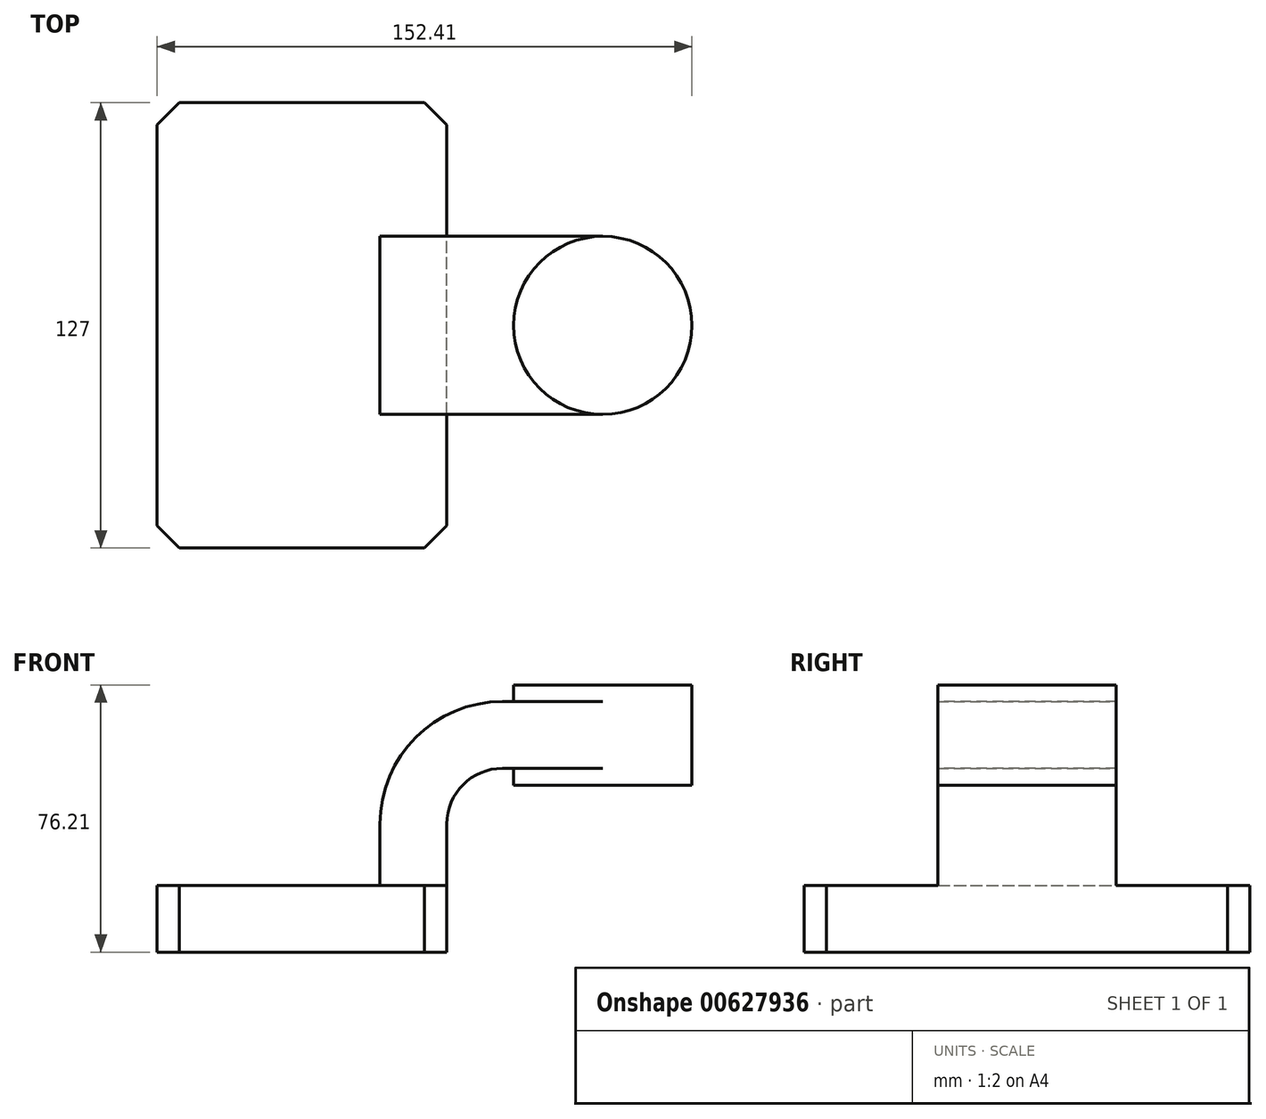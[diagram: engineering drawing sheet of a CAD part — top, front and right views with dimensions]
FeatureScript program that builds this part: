
annotation { "Feature Type Name" : "Feature", "Feature Type Description" : "" }
export const myFeature = defineFeature(function(context is Context, id is Id, definition is map)
    precondition{}
    {
        {
            var Q0;
            Q0=qCreatedBy(makeId("Front.planeOp"),FACE);
            var sketch = newSketch(context, id + "F0", { "sketchPlane" : qUnion([Q0])});
            skLineSegment(sketch, "E0.bottom", {"start": v(-41.28, -9.53) * mm, "end": v(41.28, -9.53) * mm});
            skLineSegment(sketch, "E0.top", {"start": v(-41.28, 9.53) * mm, "end": v(41.28, 9.53) * mm});
            skLineSegment(sketch, "E0.left", {"start": v(-41.28, -9.53) * mm, "end": v(-41.28, 9.53) * mm});
            skLineSegment(sketch, "E0.right", {"start": v(41.28, -9.53) * mm, "end": v(41.28, 9.53) * mm});
            skPoint(sketch, "E0.middle", {"position": v(0, 0) * mm});
            skLineSegment(sketch, "E1.bottom", {"start": v(60.33, 38.1) * mm, "end": v(111.13, 38.1) * mm});
            skLineSegment(sketch, "E1.top", {"start": v(60.33, 66.67) * mm, "end": v(111.12, 66.67) * mm});
            skLineSegment(sketch, "E1.left", {"start": v(60.33, 38.1) * mm, "end": v(60.33, 66.67) * mm});
            skLineSegment(sketch, "E1.right", {"start": v(111.12, 38.1) * mm, "end": v(111.12, 66.67) * mm});
            skPoint(sketch, "E1.middle", {"position": v(85.73, 52.39) * mm});
            skLineSegment(sketch, "E2", {"start": v(41.27, 9.53) * mm, "end": v(41.27, 27) * mm});
            skArc(sketch, "E3", {"start": v(41.27, 27) * mm, "mid": v(45.92, 38.23) * mm, "end": v(57.15, 42.88) * mm});
            skLineSegment(sketch, "E4", {"start": v(57.15, 42.88) * mm, "end": v(85.72, 42.88) * mm});
            skLineSegment(sketch, "E5.0", {"start": v(57.15, 61.93) * mm, "end": v(85.73, 61.93) * mm});
            skArc(sketch, "E5.1", {"start": v(22.22, 27) * mm, "mid": v(32.45, 51.7) * mm, "end": v(57.15, 61.93) * mm});
            skLineSegment(sketch, "E5.2", {"start": v(22.22, 9.53) * mm, "end": v(22.22, 27) * mm});
            skFitSpline(sketch, "E6", {"points": [v(-41.28, 9.53) * mm, v(57.15, 61.93) * mm], "startDerivative": vector(0.55, 109.03) * mm, "endDerivative": vector(108.88, -0.36) * mm});
            skLineSegment(sketch, "E7", {"start": v(85.73, 66.67) * mm, "end": v(85.73, 38.1) * mm});
            skSolve(sketch);
        }
        {
            var Q0;
            Q0=makeQuery(id+"F0.imprint","IMPRINT",FACE,{"disambiguationData":[TD([[makeQuery(id+"F0.imprint","IMPRINT",EDGE,{"derivedFrom":sQuery(id+"F0.wireOp",EDGE,"E0.bottom")}),1.0]])]});
            extrude(context, id + "F1", {"entities" : qUnion([Q0]), "endBound" : BoundingType.SYMMETRIC, "depth" : 127 * mm, "offsetDistance" : 25.4 * mm});
        }
        {
            var Q0;
            {var subQ1=sQuery(id+"F0.wireOp",EDGE,"E2");Q0=makeQuery(id+"F0.imprint","IMPRINT",FACE,{"disambiguationData":[TD([[makeQuery(id+"F0.imprint","IMPRINT",EDGE,{"derivedFrom":subQ1}),1.0]])]});}
            var Q1;
            {var subQ6=sQuery(id+"F0.wireOp",EDGE,"j87SMkmV-H6da-Xq5M-erbY-Rmn3BkNk3Aq3");Q1=makeQuery(id+"F0.imprint","IMPRINT",FACE,{"disambiguationData":[TD([[makeQuery(id+"F0.imprint","IMPRINT",EDGE,{"derivedFrom":subQ6}),-1.0]])]});}
            var Q2;
            {var subQ0=sQuery(id+"F0.wireOp",EDGE,"E4");var subQ1=sQuery(id+"F0.wireOp",EDGE,"E1.left");var subQ2=makeQuery(id+"F0.imprint","INTERSECT",VERTEX,{"derivedFrom":[subQ1,subQ0]});Q2=makeQuery(id+"F0.imprint","IMPRINT",FACE,{"disambiguationData":[TD([[makeQuery(id+"F0.imprint","IMPRINT",EDGE,{"disambiguationData":[TD([[subQ2,-1.0]])],"derivedFrom":subQ1}),-1.0]])]});}
            extrude(context, id + "F2", {"entities" : qUnion([Q0, Q1, Q2]), "operationType" : NewBodyOperationType.ADD, "endBound" : BoundingType.SYMMETRIC, "depth" : 50.8 * mm, "offsetDistance" : 25.4 * mm});
        }
        {
            var Q0;
            Q0=makeQuery(id+"F0.imprint","IMPRINT",FACE,{"disambiguationData":[TD([[makeQuery(id+"F0.imprint","IMPRINT",EDGE,{"derivedFrom":sQuery(id+"F0.wireOp",EDGE,"E5.1")}),1.0]])]});
            extrude(context, id + "F3", {"entities" : qUnion([Q0]), "operationType" : NewBodyOperationType.ADD, "endBound" : BoundingType.SYMMETRIC, "depth" : 15.88 * mm, "offsetDistance" : 25.4 * mm});
        }
        {
            var Q0;
            {var subQ4=sQuery(id+"F0.wireOp",EDGE,"E1.right");Q0=makeQuery(id+"F0.imprint","IMPRINT",FACE,{"disambiguationData":[TD([[makeQuery(id+"F0.imprint","IMPRINT",EDGE,{"derivedFrom":subQ4}),1.0]])]});}
            var Q1;
            Q1=sQuery(id+"F0.wireOp",EDGE,"E7");
            revolve(context, id + "F4", {"operationType" : NewBodyOperationType.ADD, "entities" : qUnion([Q0]), "axis" : qUnion([Q1]), "revolveType" : RevolveType.FULL});
        }
        {
            var Q0;
            Q0=makeQuery(id+"F1.opExtrude","CAP_EDGE",EDGE,{"disambiguationData":[OSD([sQuery(id+"F0.wireOp",EDGE,"E0.right")])],"isStart":false});
            var Q1;
            Q1=makeQuery(id+"F1.opExtrude","CAP_EDGE",EDGE,{"disambiguationData":[OSD([sQuery(id+"F0.wireOp",EDGE,"E0.left")])],"isStart":false});
            var Q2;
            Q2=makeQuery(id+"F1.opExtrude","CAP_EDGE",EDGE,{"disambiguationData":[OSD([sQuery(id+"F0.wireOp",EDGE,"E0.right")])],"isStart":true});
            var Q3;
            Q3=makeQuery(id+"F1.opExtrude","CAP_EDGE",EDGE,{"disambiguationData":[OSD([sQuery(id+"F0.wireOp",EDGE,"E0.left")])],"isStart":true});
            chamfer(context, id + "F5", {"entities" : qUnion([Q0, Q1, Q2, Q3]), "width" : 6.35 * mm, "tangentPropagation" : true});
        }
    });
